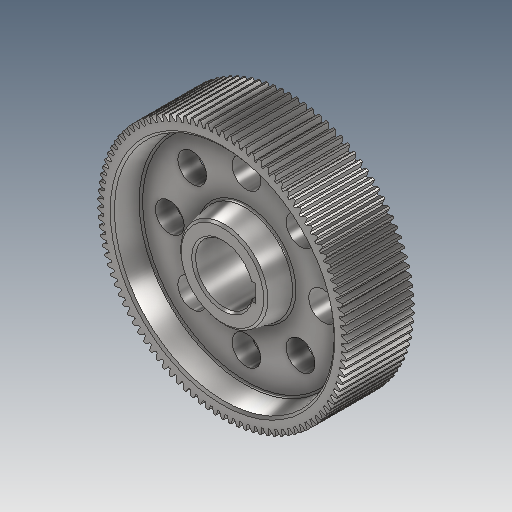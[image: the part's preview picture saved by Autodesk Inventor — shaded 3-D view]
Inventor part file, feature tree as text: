
AUTODESK INVENTOR PART (.ipt)
format: ipt  version: 2025 (Build 290162000, 162)  size: 777,216 bytes
history: native  units: mm (DEFAULTED — no unit token found)
features: other x5, sketch x5, extrude x4, plane x3, mirror x1, chamfer x1, fillet x1
ambient origin geometry x8: Origin, YZ Plane, XZ Plane, XY Plane, X Axis, Y Axis, Z Axis, Center Point
bodies: Solid1 (feature_tree)
feature tree (20):
  other  "{BB8FE430-83BF-418D-8DF9-9B323D3DB9B9}"
  extrude  "Extrusion1"  Depth=70.0mm TaperAngle=0.0deg
  plane  "Work Plane2"
  plane  "Work Plane8"
  plane  "Work Plane9"
  other  "正齿轮"
  extrude  "拉伸2"  Depth=10.0mm TaperAngle=0.0deg
  extrude  "拉伸3"  Depth=0.307999mm TaperAngle=0.0deg
  mirror  "镜像1"
  extrude  "拉伸4"  TaperAngle=0.0deg  [1 undecoded]
  chamfer  "倒角1"  Distance=166.25mm
  other  "键槽2"
  fillet  "圆角1"  [1 undecoded]
  sketch  "Sketch1"  dims[d0=260.0mm d1=70.0mm d2=0.0mm]
  other  "Srf1"
  sketch  "草图3"  dims[d16=166.25mm d17=0.0mm d34=0.307999mm]
  sketch  "草图4"  dims[d39=0.0mm d41=0.0mm]
  sketch  "草图5"  dims[d43=166.25mm d46=166.25mm d47=0.0mm d48=0.0mm d49=60.0mm d50=18.0mm d51=11.0mm d52=18.0mm d53=0.0mm d54=90.0mm d55=230.0mm d56=25.0mm d57=-2.007129mm d58=30.0mm d59=30.0mm d60=80.0mm d62=360.0deg d64=70.0mm d65=0.0mm d66=2.0mm d67=2.0mm d68=45.0deg d69=2.0mm]
  sketch  "草图 - 环形阵列1"  dims[d3=255.0mm d4=10.0mm d5=0.0mm]
  other  "轮毂键槽"
note: 2 required parameter values undecoded (feature->parameter linkage not recoverable at this tier; creation-order binding heuristic only, values carry confidence <= 0.55)
